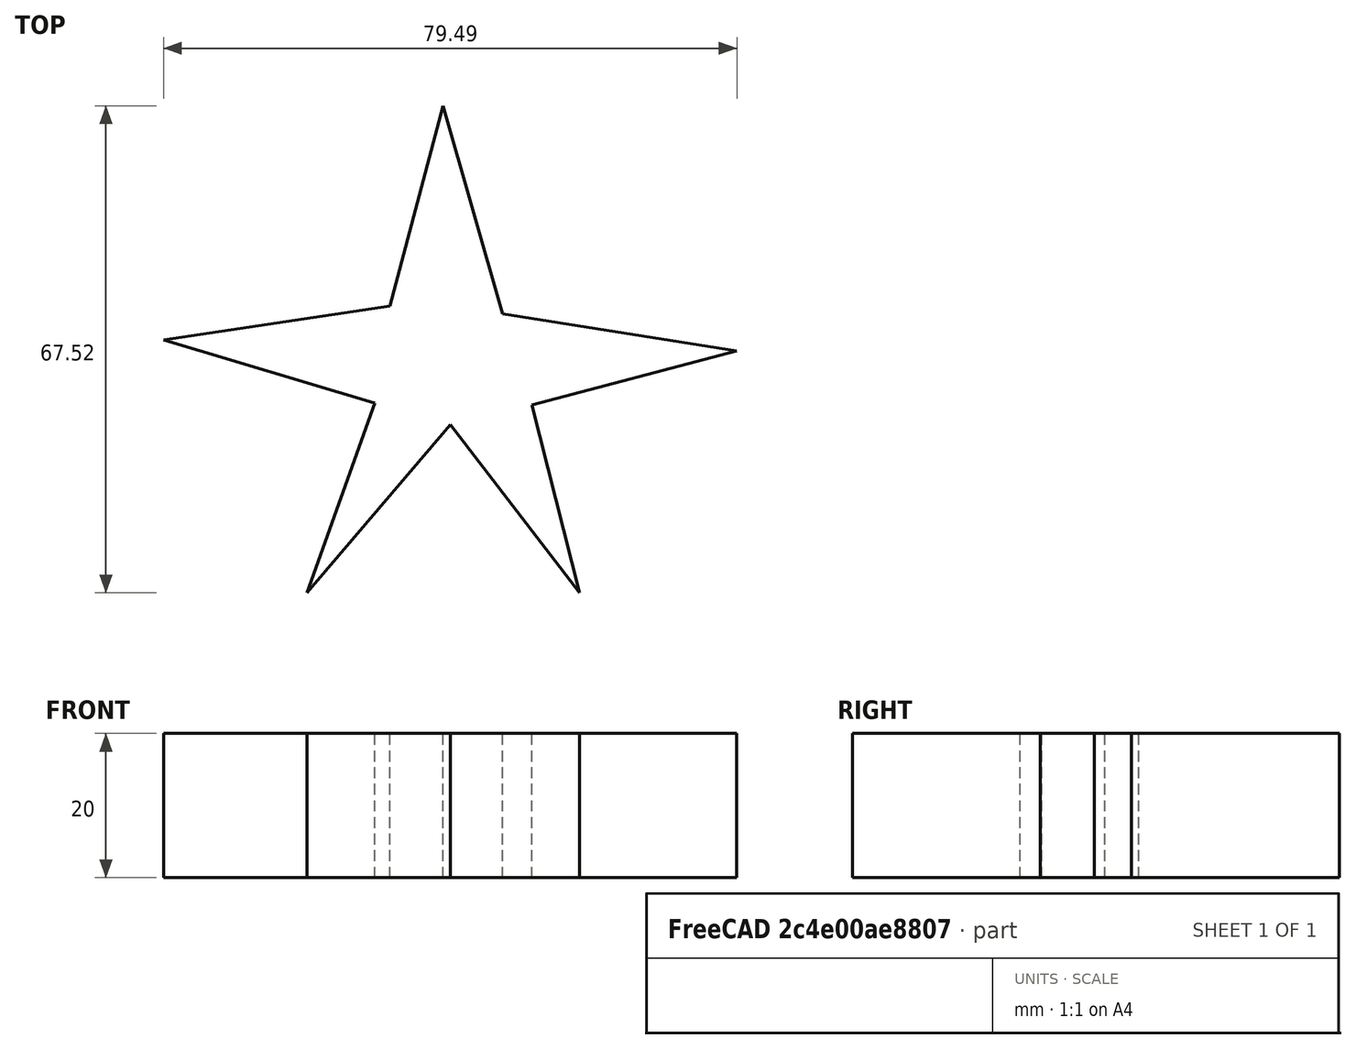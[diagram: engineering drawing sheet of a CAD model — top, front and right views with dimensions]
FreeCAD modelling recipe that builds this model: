
FCSTD DOCUMENT  (FreeCAD 1.0R39319 (Git))
Label: ojt1_t16p01_sketch_star
License: All rights reserved
LicenseURL: https://en.wikipedia.org/wiki/All_rights_reserved
objects: Sketcher::SketchObject×1, PartDesign::Pad×1, PartDesign::Body×1
note: 6 computed .brp shape members not serialized (recipe doc carries the construction recipe); baked Part::Feature solids carry a one-line shape summary decoded from their .brp

FEATURE [Sketcher::SketchObject] Sketch  label="boceto-estrella"
  ArcFitTolerance = 1e-06
  AttachmentSupport = -> [XY_Plane]
  FullyConstrained = false
  MakeInternals = false
  MapMode = 5
  sketch-geometry (10):
    g0: LineSegment StartX=9e-16 StartY=33.9744 StartZ=0 EndX=8.22649 EndY=5.12823 EndZ=0
    g1: LineSegment StartX=8.22649 StartY=5.12823 StartZ=0 EndX=40.7051 EndY=0 EndZ=0
    g2: LineSegment StartX=40.7051 StartY=0 StartZ=0 EndX=12.2863 EndY=-7.47861 EndZ=0
    g3: LineSegment StartX=12.2863 StartY=-7.47861 StartZ=0 EndX=18.9102 EndY=-33.547 EndZ=0
    g4: LineSegment StartX=18.9102 StartY=-33.547 StartZ=0 EndX=0.961537 EndY=-10.2564 EndZ=0
    g5: LineSegment StartX=0.961537 StartY=-10.2564 StartZ=0 EndX=-18.9103 EndY=-33.547 EndZ=0
    g6: LineSegment StartX=-18.9103 StartY=-33.547 StartZ=0 EndX=-9.50855 EndY=-7.26493 EndZ=0
    g7: LineSegment StartX=-9.50855 StartY=-7.26493 StartZ=0 EndX=-38.7821 EndY=1.49575 EndZ=0
    g8: LineSegment StartX=-38.7821 StartY=1.49575 StartZ=0 EndX=-7.3718 EndY=6.19661 EndZ=0
    g9: LineSegment StartX=-7.3718 StartY=6.19661 StartZ=0 EndX=9e-16 EndY=33.9744 EndZ=0
  constraints (12):
    c: PointOnObject(g0,g-2)
    c: Coincident(g0,g1)
    c: PointOnObject(g1,g-1)
    c: Coincident(g1,g2)
    c: Coincident(g2,g3)
    c: Coincident(g3,g4)
    c: Coincident(g4,g5)
    c: Coincident(g5,g6)
    c: Coincident(g6,g7)
    c: Coincident(g7,g8)
    c: Coincident(g8,g9)
    c: Coincident(g9,g0)
FEATURE [PartDesign::Pad] Pad  label="estrella"
  Direction = (0,0,1)
  Length = 20
  Length2 = 10
  Profile = -> Sketch
  ReferenceAxis = -> Sketch [N_Axis]
  Refine = true
  Suppressed = false
  Type = 0
FEATURE [PartDesign::Body] Body
  AllowCompound = false
  Group = -> [Sketch,Pad]
  Origin = -> Origin
  Tip = -> Pad
